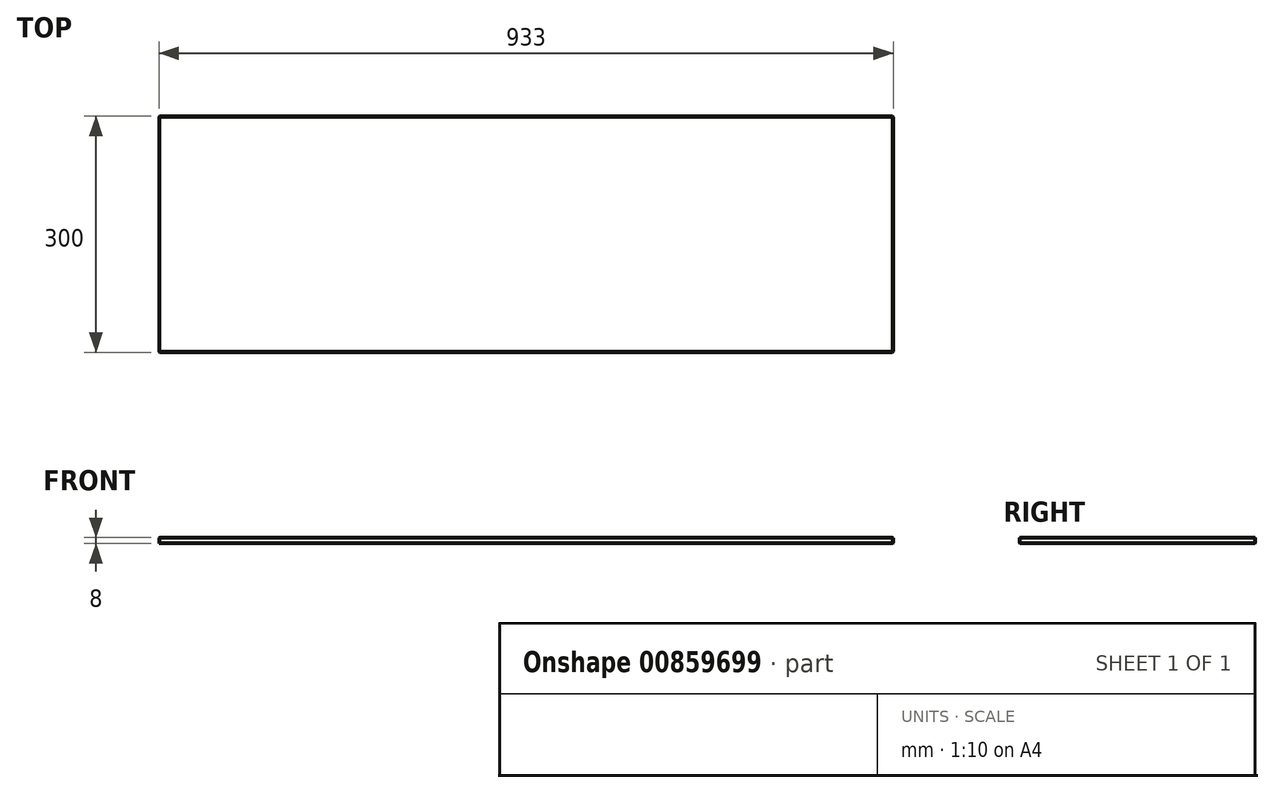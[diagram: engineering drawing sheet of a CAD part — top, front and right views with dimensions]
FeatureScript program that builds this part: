
annotation { "Feature Type Name" : "Feature", "Feature Type Description" : "" }
export const myFeature = defineFeature(function(context is Context, id is Id, definition is map)
    precondition{}
    {
        {
            var Q0;
            Q0=qCreatedBy(makeId("Top.planeOp"),FACE);
            var sketch = newSketch(context, id + "F0", { "sketchPlane" : qUnion([Q0])});
            skLineSegment(sketch, "E0.bottom", {"start": v(-466.5, 150) * mm, "end": v(466.5, 150) * mm});
            skLineSegment(sketch, "E0.top", {"start": v(-466.5, -150) * mm, "end": v(466.5, -150) * mm});
            skLineSegment(sketch, "E0.left", {"start": v(-466.5, 150) * mm, "end": v(-466.5, -150) * mm});
            skLineSegment(sketch, "E0.right", {"start": v(466.5, 150) * mm, "end": v(466.5, -150) * mm});
            skPoint(sketch, "E0.middle", {"position": v(0, 0) * mm});
            skSolve(sketch);
        }
        {
            var Q0;
            Q0=makeQuery(id+"F0.imprint","IMPRINT",FACE,{"disambiguationData":[TD([[makeQuery(id+"F0.imprint","IMPRINT",EDGE,{"derivedFrom":sQuery(id+"F0.wireOp",EDGE,"E0.bottom")}),-1.0]])]});
            extrude(context, id + "F1", {"entities" : qUnion([Q0]), "endBound" : BoundingType.SYMMETRIC, "depth" : 8 * mm, "offsetDistance" : 25 * mm});
        }
        {
            var Q0;
            Q0=makeQuery(id+"F1.opExtrude","CAP_EDGE",EDGE,{"disambiguationData":[OSD([sQuery(id+"F0.wireOp",EDGE,"E0.right")])],"isStart":true});
            var Q1;
            Q1=makeQuery(id+"F1.opExtrude","CAP_EDGE",EDGE,{"disambiguationData":[OSD([sQuery(id+"F0.wireOp",EDGE,"E0.top")])],"isStart":true});
            var Q2;
            Q2=makeQuery(id+"F1.opExtrude","CAP_EDGE",EDGE,{"disambiguationData":[OSD([sQuery(id+"F0.wireOp",EDGE,"E0.left")])],"isStart":true});
            var Q3;
            Q3=makeQuery(id+"F1.opExtrude","CAP_EDGE",EDGE,{"disambiguationData":[OSD([sQuery(id+"F0.wireOp",EDGE,"E0.bottom")])],"isStart":true});
            chamfer(context, id + "F2", {"entities" : qUnion([Q0, Q1, Q2, Q3]), "width" : 1 * mm, "tangentPropagation" : true});
        }
        {
            var Q0;
            Q0=makeQuery(id+"F1.opExtrude","SWEPT_EDGE",EDGE,{"disambiguationData":[OSD([sQuery(id+"F0.wireOp",EDGE,"E0.top"),sQuery(id+"F0.wireOp",EDGE,"E0.right")])]});
            chamfer(context, id + "F3", {"entities" : qUnion([Q0]), "width" : 1 * mm, "tangentPropagation" : true});
        }
        {
            var Q0;
            Q0=makeQuery(id+"F1.opExtrude","SWEPT_EDGE",EDGE,{"disambiguationData":[OSD([sQuery(id+"F0.wireOp",EDGE,"E0.bottom"),sQuery(id+"F0.wireOp",EDGE,"E0.left")])]});
            chamfer(context, id + "F4", {"entities" : qUnion([Q0]), "width" : 1 * mm, "tangentPropagation" : true});
        }
        {
            var Q0;
            Q0=makeQuery(id+"F1.opExtrude","SWEPT_EDGE",EDGE,{"disambiguationData":[OSD([sQuery(id+"F0.wireOp",EDGE,"E0.top"),sQuery(id+"F0.wireOp",EDGE,"E0.left")])]});
            chamfer(context, id + "F5", {"entities" : qUnion([Q0]), "width" : 1 * mm, "tangentPropagation" : true});
        }
        {
            var Q0;
            Q0=makeQuery(id+"F1.opExtrude","SWEPT_EDGE",EDGE,{"disambiguationData":[OSD([sQuery(id+"F0.wireOp",EDGE,"E0.bottom"),sQuery(id+"F0.wireOp",EDGE,"E0.right")])]});
            chamfer(context, id + "F6", {"entities" : qUnion([Q0]), "width" : 1 * mm, "tangentPropagation" : true});
        }
        {
            var Q0;
            Q0=makeQuery(id+"F1.opExtrude","CAP_EDGE",EDGE,{"disambiguationData":[OSD([sQuery(id+"F0.wireOp",EDGE,"E0.top")])],"isStart":false});
            var Q1;
            Q1=makeQuery(id+"F1.opExtrude","CAP_EDGE",EDGE,{"disambiguationData":[OSD([sQuery(id+"F0.wireOp",EDGE,"E0.right")])],"isStart":false});
            var Q2;
            Q2=makeQuery(id+"F1.opExtrude","CAP_EDGE",EDGE,{"disambiguationData":[OSD([sQuery(id+"F0.wireOp",EDGE,"E0.bottom")])],"isStart":false});
            var Q3;
            Q3=makeQuery(id+"F1.opExtrude","CAP_EDGE",EDGE,{"disambiguationData":[OSD([sQuery(id+"F0.wireOp",EDGE,"E0.left")])],"isStart":false});
            chamfer(context, id + "F7", {"entities" : qUnion([Q0, Q1, Q2, Q3]), "width" : 1 * mm, "tangentPropagation" : true});
        }
    });
